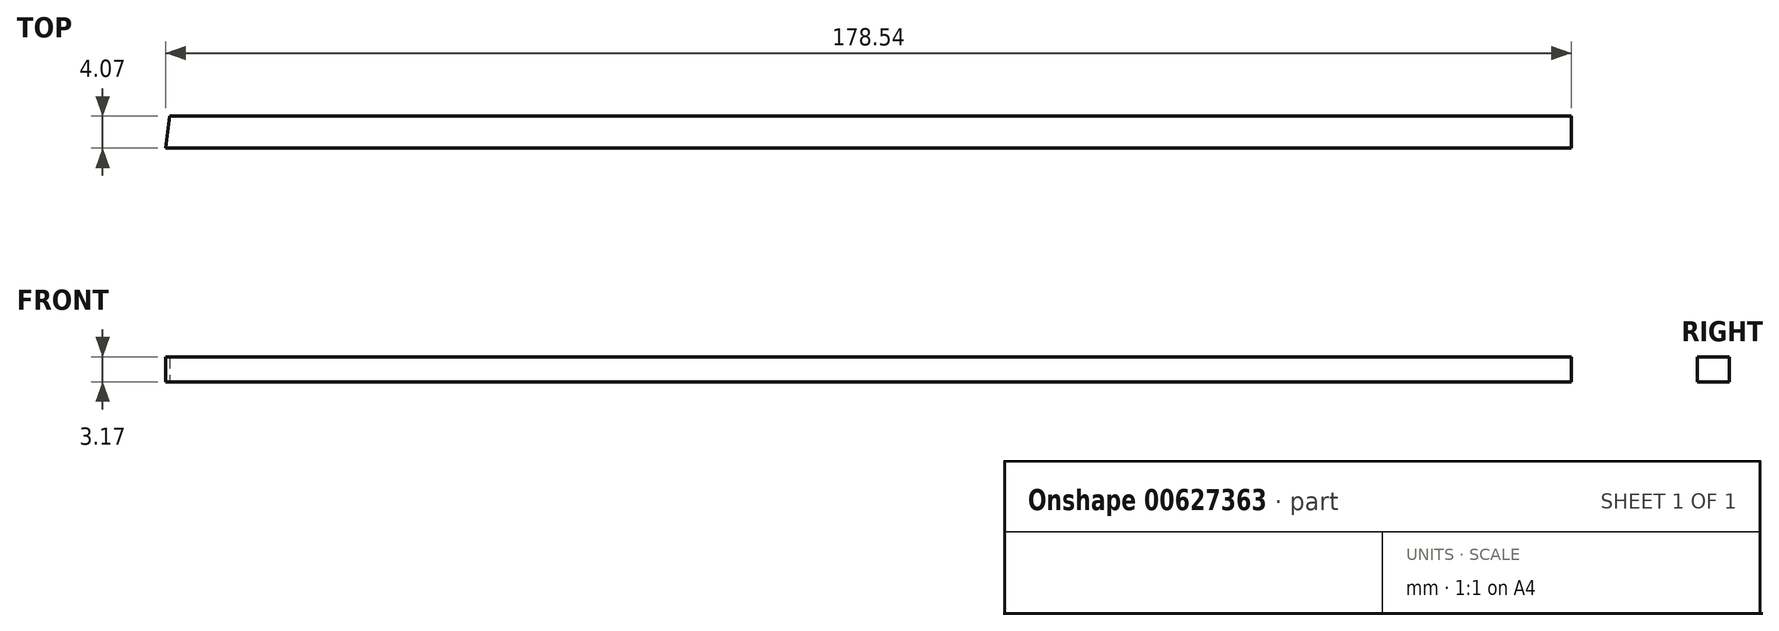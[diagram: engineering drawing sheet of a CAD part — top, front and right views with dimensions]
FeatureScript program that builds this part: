
annotation { "Feature Type Name" : "Feature", "Feature Type Description" : "" }
export const myFeature = defineFeature(function(context is Context, id is Id, definition is map)
    precondition{}
    {
        {
            var Q0;
            Q0=qCreatedBy(makeId("Top.planeOp"),FACE);
            var sketch = newSketch(context, id + "F0", { "sketchPlane" : qUnion([Q0])});
            skLineSegment(sketch, "E0", {"start": v(-155.5, 4.07) * mm, "end": v(22.56, 4.07) * mm});
            skLineSegment(sketch, "E1", {"start": v(22.56, 4.07) * mm, "end": v(22.56, 0) * mm});
            skLineSegment(sketch, "E2", {"start": v(22.56, 0) * mm, "end": v(-155.98, 0) * mm});
            skLineSegment(sketch, "E3", {"start": v(-155.98, 0) * mm, "end": v(-155.5, 4.07) * mm});
            skSolve(sketch);
        }
        {
            var Q0;
            Q0=makeQuery(id+"F0.imprint","IMPRINT",FACE,{"disambiguationData":[TD([[makeQuery(id+"F0.imprint","IMPRINT",EDGE,{"derivedFrom":sQuery(id+"F0.wireOp",EDGE,"E0")}),-1.0]])]});
            extrude(context, id + "F1", {"entities" : qUnion([Q0]), "depth" : 3.17 * mm, "offsetDistance" : 25.4 * mm});
        }
    });
